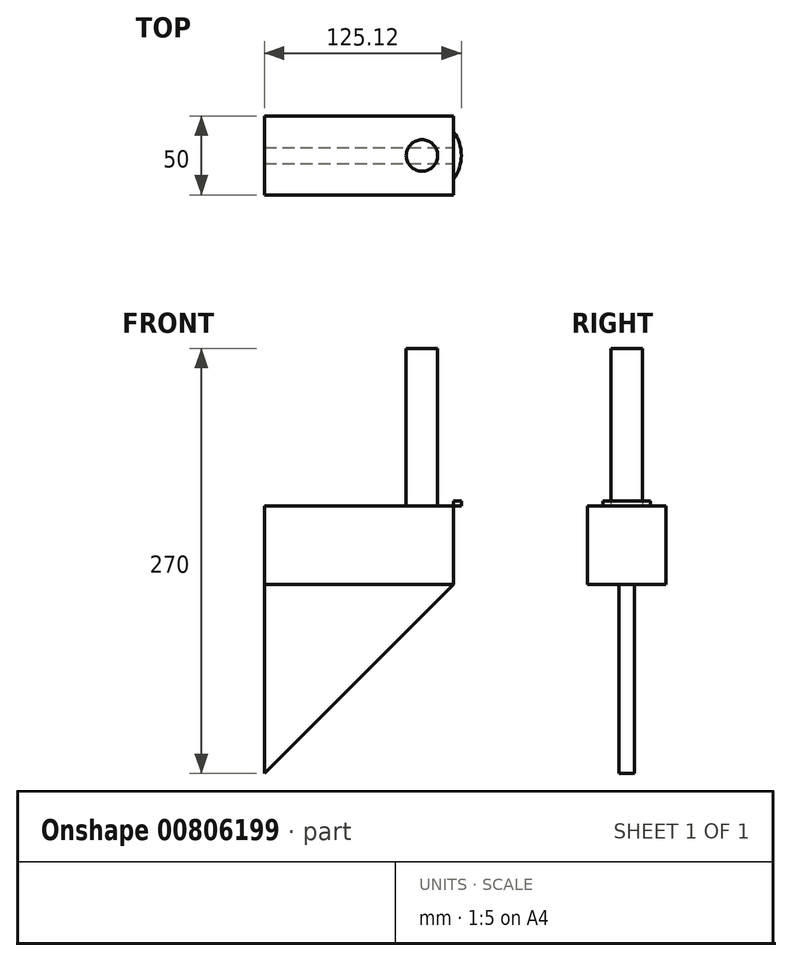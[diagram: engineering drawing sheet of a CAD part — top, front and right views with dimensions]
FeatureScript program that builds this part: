
annotation { "Feature Type Name" : "Feature", "Feature Type Description" : "" }
export const myFeature = defineFeature(function(context is Context, id is Id, definition is map)
    precondition{}
    {
        {
            var Q0;
            Q0=qCreatedBy(makeId("Top.planeOp"),FACE);
            var sketch = newSketch(context, id + "F0", { "sketchPlane" : qUnion([Q0])});
            skLineSegment(sketch, "E0.bottom", {"start": v(-60, -25) * mm, "end": v(60, -25) * mm});
            skLineSegment(sketch, "E0.top", {"start": v(-60, 25) * mm, "end": v(60, 25) * mm});
            skLineSegment(sketch, "E0.left", {"start": v(-60, -25) * mm, "end": v(-60, 25) * mm});
            skLineSegment(sketch, "E0.right", {"start": v(60, -25) * mm, "end": v(60, 25) * mm});
            skPoint(sketch, "E0.middle", {"position": v(0, 0) * mm});
            skSolve(sketch);
        }
        {
            var Q0;
            Q0=qSketchRegion(id+"F0",true);
            var Q1;
            Q1=makeQuery(id+"F0.imprint","IMPRINT",FACE,{"disambiguationData":[TD([[makeQuery(id+"F0.imprint","IMPRINT",EDGE,{"derivedFrom":sQuery(id+"F0.wireOp",EDGE,"E0.bottom")}),1.0]])]});
            extrude(context, id + "F1", {"entities" : qUnion([Q0, Q1]), "depth" : 50 * mm, "offsetDistance" : 25 * mm});
        }
        {
            var Q0;
            Q0=makeQuery(id+"F1.opExtrude","CAP_FACE",FACE,{"disambiguationData":[OSD([sQuery(id+"F0.wireOp",EDGE,"E0.bottom"),sQuery(id+"F0.wireOp",EDGE,"E0.top"),sQuery(id+"F0.wireOp",EDGE,"E0.left"),sQuery(id+"F0.wireOp",EDGE,"E0.right")])],"isStart":false});
            var sketch = newSketch(context, id + "F2", { "sketchPlane" : qUnion([Q0])});
            skLineSegment(sketch, "E1", {"start": v(-60, 0) * mm, "end": v(40, 0) * mm});
            skCircle(sketch, "E2", {"center": v(40, 0) * mm, "radius": 10 * mm});
            skSolve(sketch);
        }
        {
            var Q0;
            Q0=qSketchRegion(id+"F2",true);
            extrude(context, id + "F3", {"entities" : qUnion([Q0]), "operationType" : NewBodyOperationType.ADD, "depth" : 100 * mm, "offsetDistance" : 25 * mm});
        }
        {
            var Q0;
            Q0=qCreatedBy(makeId("Front.planeOp"),FACE);
            var sketch = newSketch(context, id + "F4", { "sketchPlane" : qUnion([Q0])});
            skLineSegment(sketch, "E3", {"start": v(-60.12, 0) * mm, "end": v(59.88, 0) * mm});
            skLineSegment(sketch, "E4", {"start": v(-60.12, 0) * mm, "end": v(-60.12, -120) * mm});
            skLineSegment(sketch, "E5", {"start": v(-60.12, -120) * mm, "end": v(59.88, 0) * mm});
            skSolve(sketch);
        }
        {
            var Q0;
            Q0=makeQuery(id+"F4.imprint","IMPRINT",FACE,{"disambiguationData":[TD([[makeQuery(id+"F4.imprint","IMPRINT",EDGE,{"derivedFrom":sQuery(id+"F4.wireOp",EDGE,"E3")}),-1.0]])]});
            extrude(context, id + "F5", {"entities" : qUnion([Q0]), "operationType" : NewBodyOperationType.ADD, "endBound" : BoundingType.SYMMETRIC, "depth" : 10 * mm, "offsetDistance" : 25 * mm});
        }
        {
            var Q0;
            Q0=makeQuery(id+"F1.opExtrude","CAP_FACE",FACE,{"disambiguationData":[OSD([sQuery(id+"F0.wireOp",EDGE,"E0.bottom"),sQuery(id+"F0.wireOp",EDGE,"E0.top"),sQuery(id+"F0.wireOp",EDGE,"E0.left"),sQuery(id+"F0.wireOp",EDGE,"E0.right")])],"isStart":false});
            var sketch = newSketch(context, id + "F6", { "sketchPlane" : qUnion([Q0])});
            skCircle(sketch, "E6", {"center": v(40, 0) * mm, "radius": 25 * mm});
            skSolve(sketch);
        }
        {
            var Q0;
            Q0=makeQuery(id+"F6.imprint","IMPRINT",FACE,{"disambiguationData":[TD([[makeQuery(id+"F6.imprint","IMPRINT",EDGE,{"derivedFrom":makeQuery(id+"F3.opExtrude","CAP_EDGE",EDGE,{"disambiguationData":[OSD([sQuery(id+"F2.wireOp",EDGE,"E2")])],"isStart":true})}),-1.0]])]});
            var Q1;
            {var subQ0=sQuery(id+"F6.wireOp",EDGE,"E6");var subQ1=makeQuery(id+"F1.opExtrude","CAP_EDGE",EDGE,{"disambiguationData":[OSD([sQuery(id+"F0.wireOp",EDGE,"E0.right")])],"isStart":false});var subQ2=makeQuery(id+"F6.imprint","INTERSECT",VERTEX,{"disambiguationData":[OD(0.0)],"derivedFrom":[subQ1,subQ0]});Q1=makeQuery(id+"F6.imprint","IMPRINT",FACE,{"disambiguationData":[TD([[makeQuery(id+"F6.imprint","IMPRINT",EDGE,{"disambiguationData":[TD([[subQ2,1.0]])],"derivedFrom":subQ0}),1.0]])]});}
            extrude(context, id + "F7", {"entities" : qUnion([Q0, Q1]), "operationType" : NewBodyOperationType.ADD, "depth" : 3 * mm, "offsetDistance" : 25 * mm});
        }
    });
